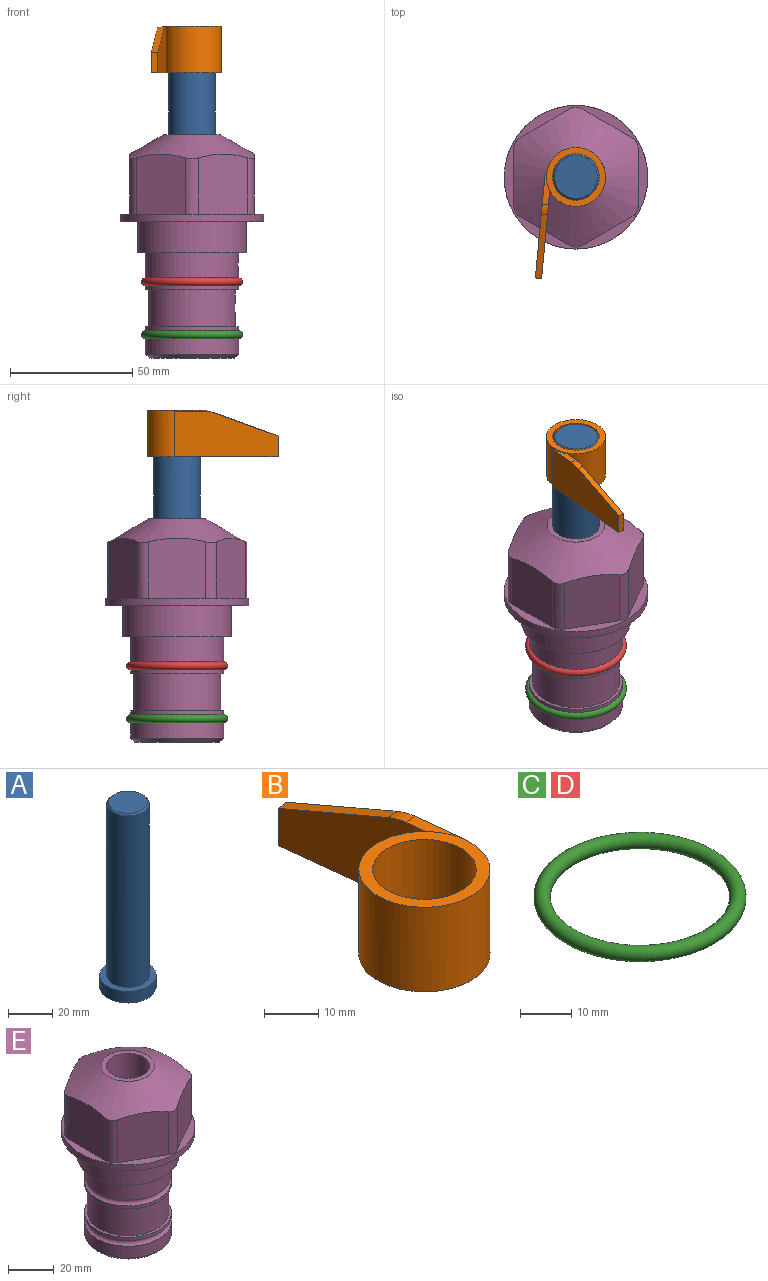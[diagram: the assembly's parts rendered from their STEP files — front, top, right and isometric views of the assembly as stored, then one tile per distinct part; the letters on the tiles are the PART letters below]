
ASSEMBLY  parts=5 mates=3
PART A: 6 faces, bbox 25.4x25.4x101.6 mm
  f0: plane 17.46x17.46mm, normal (0,0,1), area 239.5mm2, adj f5
  f1: plane 25.4x25.4mm, normal (0,0,-1), area 506.7mm2, adj f2
  f2: cylinder r=12.7mm len=25.4mm, axis (0,0,1), area 506.7mm2, adj f1,f3
  f3: plane 25.4x25.4mm, normal (0,0,1), area 221.7mm2, adj f2,f4
  f4: cylinder r=9.53mm len=94.46mm, axis (0,0,1), area 5653mm2, adj f3,f5
  f5: cone r=8.73mm half-angle=45deg, axis (0,0,-1), area 64.4mm2, adj f0,f4
PART B: 11 faces, bbox 24.7x55.8x19.1 mm
  f0: plane 24.13x24.13mm, normal (0,0,1), area 172.3mm2, adj f3,f10
  f1: plane 55.81x24.69mm, normal (0,0,-1), area 272.1mm2, adj f2,f3,f7,f8,f9,f10
  f2: plane 42.34x18.55mm, normal (0.99,0.11,0), area 647mm2, adj f1,f4,f5,f6,f7,f8
  f3: cylinder r=9.53mm len=19.05mm, axis (0,0,-1), area 1140.1mm2, adj f0,f1
  f4: plane 12.35x3.9mm, normal (0,0,1), area 23mm2, adj f2,f5,f7,f9,f10
  f5: bspline ~4.45x2.99mm, area 10.9mm2, adj f2,f4,f6,f9
  f6: plane 26.16x9.42mm, normal (-0.04,0.34,0.94), area 70.3mm2, adj f2,f5,f8,f9
  f7: plane 18.54x0.63mm, normal (0.11,-0.99,0), area 11.8mm2, adj f1,f2,f4,f10
  f8: plane 8.39x2.52mm, normal (-0.11,0.99,0), area 21.3mm2, adj f1,f2,f6,f9
  f9: plane 35.87x18.54mm, normal (-0.99,-0.11,0), area 526.3mm2, adj f1,f4,f5,f6,f8,f10
  f10: cylinder r=12.06mm len=24.13mm, axis (0,0,-1), area 1316.7mm2, adj f0,f1,f4,f7,f9
PART C: 1 faces, bbox 44.7x44.7x3.2 mm
  f0: torus R=19.05mm, axis (0,0,1), area 1193.9mm2
PART D: same geometry as C
PART E: 36 faces, bbox 58.7x58.7x91.2 mm
  f0: cylinder r=17.78mm len=35.56mm, axis (0,0,1), area 1670.8mm2, adj f23,f24,f31
  f1: cylinder r=19.05mm len=38.1mm, axis (0,0,1), area 1191.9mm2, adj f26,f27,f30
  f2: plane 58.66x58.66mm, normal (0,0,-1), area 1150.6mm2, adj f3,f28
  f3: cylinder r=29.33mm len=58.66mm, axis (0,0,-1), area 585.1mm2, adj f2,f4
  f4: plane 58.66x58.66mm, normal (0,0,1), area 475.9mm2, adj f3,f5,f6,f7,f8,f9,f10,f11
  f5: plane 24.5x20.32mm, normal (-0.5,0.87,0), area 562.8mm2, adj f4,f15,f16,f17
  f6: plane 24.5x20.32mm, normal (0.5,0.87,0), area 562.8mm2, adj f4,f14,f15,f17
  f7: plane 24.5x23.48mm, normal (1,0,0), area 562.8mm2, adj f4,f13,f14,f17
  f8: plane 24.5x20.32mm, normal (0.5,-0.87,0), area 562.8mm2, adj f4,f12,f13,f17
  f9: plane 24.5x20.32mm, normal (-0.5,-0.87,0), area 562.8mm2, adj f4,f11,f12,f17
  f10: plane 24.5x23.48mm, normal (-1,0,0), area 562.8mm2, adj f4,f11,f16,f17
  f11: cylinder r=5.08mm len=23.01mm, axis (0,0,-1), area 121.2mm2, adj f4,f9,f10,f17
  f12: cylinder r=5.08mm len=23.01mm, axis (0,0,-1), area 121.2mm2, adj f4,f8,f9,f17
  f13: cylinder r=5.08mm len=23.01mm, axis (0,0,-1), area 121.2mm2, adj f4,f7,f8,f17
  f14: cylinder r=5.08mm len=23.01mm, axis (0,0,-1), area 121.2mm2, adj f4,f6,f7,f17
  f15: cylinder r=5.08mm len=23.01mm, axis (0,0,-1), area 121.2mm2, adj f4,f5,f6,f17
  f16: cylinder r=5.08mm len=23.01mm, axis (0,0,-1), area 121.2mm2, adj f4,f5,f10,f17
  f17: cone r=11.73mm half-angle=60deg, axis (0,0,-1), area 2071.8mm2, adj f5,f6,f7,f8,f9,f10,f11,f12
  f18: plane 23.46x23.46mm, normal (0,0,1), area 147.4mm2, adj f17,f35
  f19: plane 34.93x34.93mm, normal (0,0,-1), area 958mm2, adj f29
  f20: cylinder r=19.05mm len=38.1mm, axis (0,0,1), area 760.1mm2, adj f21,f29
  f21: torus R=19.05mm, axis (0,0,1), area 565.3mm2, adj f20,f22
  f22: cylinder r=19.05mm len=38.1mm, axis (0,0,1), area 190mm2, adj f21,f23
  f23: plane 38.1x38.1mm, normal (0,0,1), area 146.9mm2, adj f0,f22
  f24: plane 38.1x38.1mm, normal (0,0,-1), area 146.9mm2, adj f0,f25
  f25: cylinder r=19.05mm len=38.1mm, axis (0,0,1), area 190mm2, adj f24,f26
  f26: torus R=19.05mm, axis (0,0,1), area 565.3mm2, adj f1,f25
  f27: plane 44.45x44.45mm, normal (0,0,-1), area 411.7mm2, adj f1,f28
  f28: cylinder r=22.23mm len=44.45mm, axis (0,0,1), area 1773.5mm2, adj f2,f27
  f29: cone r=19.05mm half-angle=45deg, axis (0,0,1), area 257.5mm2, adj f19,f20
  f30: cylinder r=3.17mm len=6.75mm, axis (-1,0,0), area 128mm2, adj f1,f33
  f31: cylinder r=3.17mm len=6.35mm, axis (-1,0,0), area 102.5mm2, adj f0,f33
  f32: plane 25.4x25.4mm, normal (0,0,1), area 506.7mm2, adj f33
  f33: cylinder r=12.7mm len=66.42mm, axis (0,0,-1), area 5236.2mm2, adj f30,f31,f32,f34
  f34: cone r=9.53mm half-angle=30deg, axis (0,0,-1), area 443.4mm2, adj f33,f35
  f35: cylinder r=9.53mm len=19.05mm, axis (0,0,-1), area 849mm2, adj f18,f34
PLACE A rot(axis=(0,0,-1),101.7deg) t=(0,0,6.38)mm
PLACE B rot(axis=(0,0,1),168.3deg) t=(0,0,60.99)mm
PLACE C t=(0,0,-21.59)mm
PLACE D at identity
PLACE E at identity fixed
MATE fastened C.f0 <-> E.f0  axis (0,0,1) through (0,0,-46.1)mm
MATE cylindrical A.f2 <-> E.f0  axis (0,0,1) through (0,0,32.01)mm
MATE fastened B.f3 <-> A.f2  axis (0,0,1) through (0,0,80.04)mm
